# Revit family: Beam Hangers-Side
name_source: partatom
category: Detail Items
revit_build: Autodesk Revit Architecture 2012 (Build: 20110210_1515)
units: mm (PartAtom-declared; Revit-internal decimal feet)

## types (28) — shared parameters
Flange = 2 1/2"
Gauge = 12

## per-type parameters (varying)
| type | Base | Finish | Height | Joist | Keynote | Width |
| B38 | 2" | Galvanize | 7 1/8" | 3x8 | 06 05 23.D1 | 2 9/16" |
| HHB816 | 3" | Gray Paint | 15" | 8x16 | 06 05 23.D28 | 7 1/2" |
| B310 | 2" | Galvanize | 9 1/8" | 3x10 | 06 05 23.D2 | 2 9/16" |
| B312 | 2 3/8" | Galvanize | 11" | 3x12 | 06 05 23.D3 | 2 9/16" |
| B314 | 3" | Galvanize | 13" | 3x14 | 06 05 23.D4 | 2 9/16" |
| B316 | 3" | Galvanize | 15" | 3x16 | 06 05 23.D5 | 2 9/16" |
| B48 | 2" | Galvanize | 7 1/8" | 4x8 | 06 05 23.D6 | 3 9/16" |
| B410 | 2" | Galvanize | 9 1/8" | 4x10 | 06 05 23.D7 | 3 9/16" |
| B412 | 2 3/8" | Galvanize | 11" | 4x12 | 06 05 23.D8 | 3 9/16" |
| HB412 | 3" | Galvanize | 11" | 4x12 | 06 05 23.D9 | 3 9/16" |
| HHB412 | 3" | Gray Paint | 11" | 4x12 | 06 05 23.D10 | 3 9/16" |
| B414 | 2 3/8" | Galvanize | 13" | 4x14 | 06 05 23.D11 | 3 9/16" |
| HB414 | 3" | Galvanize | 13" | 4x14 | 06 05 23.D12 | 3 9/16" |
| HHB414 | 3" | Gray Paint | 13" | 4x14 | 06 05 23.D13 | 3 9/16" |
| B416 | 2 3/8" | Galvanize | 15" | 4x16 | 06 05 23.D14 | 3 9/16" |
| HB416 | 3" | Galvanize | 15" | 4x16 | 06 05 23.D15 | 3 9/16" |
| HHB416 | 3" | Gray Paint | 15" | 4x16 | 06 05 23.D16 | 3 9/16" |
| HHB68 | 2" | Gray Paint | 7 1/8" | 6x8 | 06 05 23.D17 | 5 1/2" |
| B610 | 2 3/8" | Galvanize | 9 1/8" | 6x10 | 06 05 23.D18 | 5 1/2" |
| HHB610 | 2" | Gray Paint | 9 1/8" | 6x10 | 06 05 23.D19 | 5 1/2" |
| B612 | 2 3/8" | Galvanize | 11" | 6x12 | 06 05 23.D20 | 5 1/2" |
| HHB612 | 3" | Gray Paint | 11" | 6x12 | 06 05 23.D21 | 5 1/2" |
| B614 | 2 3/8" | Galvanize | 13" | 6x14 | 06 05 23.D22 | 5 1/2" |
| HHB614 | 3" | Gray Paint | 13" | 6x14 | 06 05 23.D23 | 5 1/2" |
| B616 | 2 3/8" | Galvanize | 15" | 6x16 | 06 05 23.D24 | 5 1/2" |
| HHB616 | 3" | Gray Paint | 15" | 6x16 | 06 05 23.D25 | 5 1/2" |
| HHB814 | 3" | Gray Paint | 13" | 8x14 | 06 05 23.D27 | 7 1/2" |
| HHB812 | 3" | Gray Paint | 11" | 8x12 | 06 05 23.D26 | 7 1/2" |

## geometry (parser evidence)
native form markers: Sweep x1
no freeform markers — native parametric forms only
